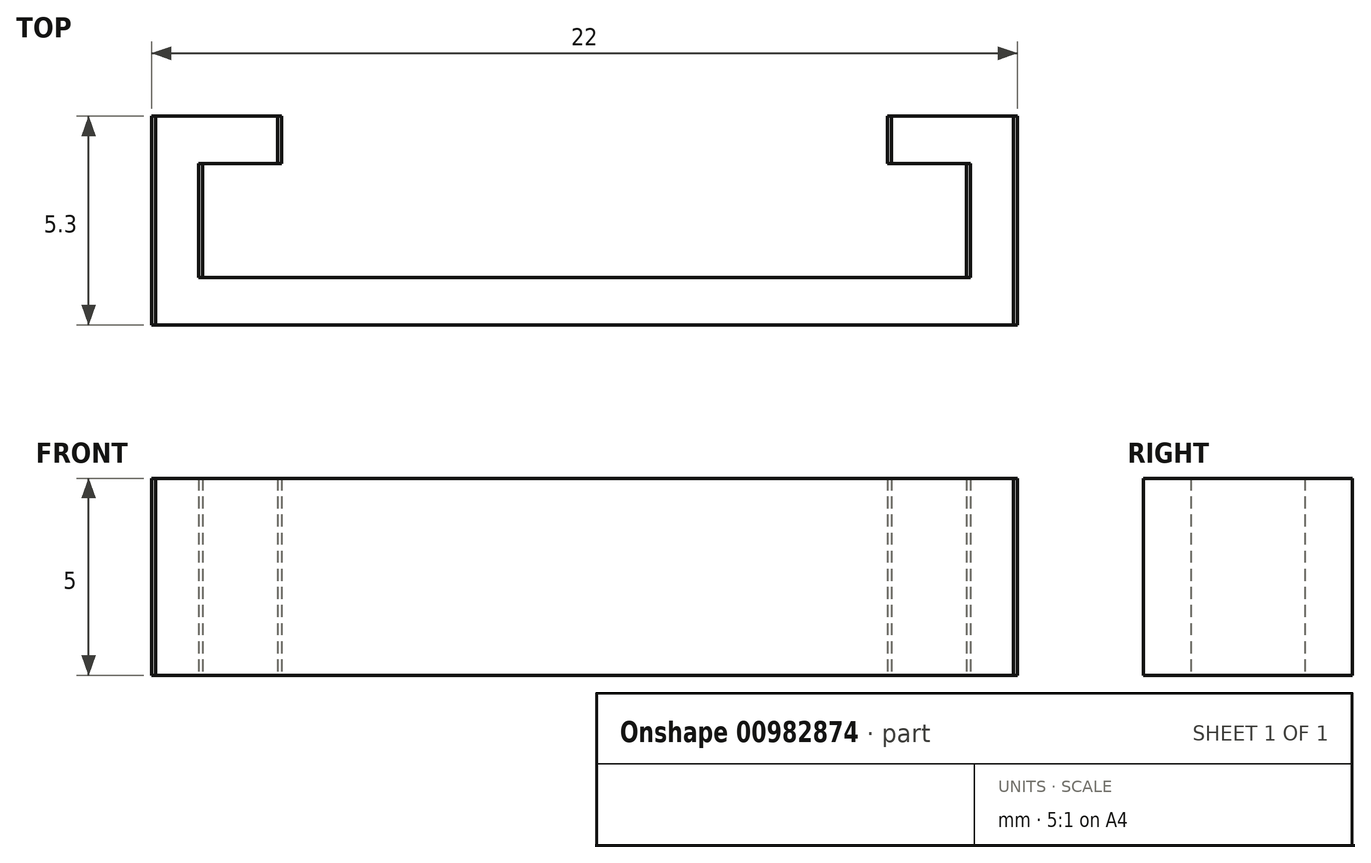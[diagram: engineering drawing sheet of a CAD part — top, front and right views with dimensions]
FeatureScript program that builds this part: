
annotation { "Feature Type Name" : "Feature", "Feature Type Description" : "" }
export const myFeature = defineFeature(function(context is Context, id is Id, definition is map)
    precondition{}
    {
        {
            var Q0;
            Q0=qCreatedBy(makeId("Top.planeOp"),FACE);
            var sketch = newSketch(context, id + "F0", { "sketchPlane" : qUnion([Q0])});
            skLineSegment(sketch, "E0", {"start": v(0, -39.9) * mm, "end": v(0, 36.9) * mm, "construction": true});
            skLineSegment(sketch, "E1", {"start": v(0, 0) * mm, "end": v(-11, 0) * mm});
            skLineSegment(sketch, "E2", {"start": v(-11, 0) * mm, "end": v(-11, 5.3) * mm});
            skLineSegment(sketch, "E3", {"start": v(-11, 5.3) * mm, "end": v(-7.8, 5.3) * mm});
            skLineSegment(sketch, "E4", {"start": v(-7.8, 5.3) * mm, "end": v(-7.8, 4.1) * mm});
            skLineSegment(sketch, "E5", {"start": v(-7.8, 4.1) * mm, "end": v(-9.8, 4.1) * mm});
            skLineSegment(sketch, "E6", {"start": v(-9.8, 4.1) * mm, "end": v(-9.8, 1.2) * mm});
            skLineSegment(sketch, "E7", {"start": v(-9.8, 1.2) * mm, "end": v(0, 1.2) * mm});
            skLineSegment(sketch, "E8", {"start": v(0, 1.2) * mm, "end": v(0, 0) * mm});
            skLineSegment(sketch, "E9.MirrorCS", {"start": v(9.8, 1.2) * mm, "end": v(0, 1.2) * mm});
            skLineSegment(sketch, "E10.MirrorCS", {"start": v(0, 0) * mm, "end": v(11, 0) * mm});
            skLineSegment(sketch, "E11.MirrorCS", {"start": v(11, 0) * mm, "end": v(11, 5.3) * mm});
            skLineSegment(sketch, "E12.MirrorCS", {"start": v(11, 5.3) * mm, "end": v(7.8, 5.3) * mm});
            skLineSegment(sketch, "E13.MirrorCS", {"start": v(7.8, 5.3) * mm, "end": v(7.8, 4.1) * mm});
            skLineSegment(sketch, "E14.MirrorCS", {"start": v(7.8, 4.1) * mm, "end": v(9.8, 4.1) * mm});
            skLineSegment(sketch, "E15.MirrorCS", {"start": v(9.8, 4.1) * mm, "end": v(9.8, 1.2) * mm});
            skSolve(sketch);
        }
        {
            var Q0;
            Q0=makeQuery(id+"F0.imprint","IMPRINT",FACE,{"disambiguationData":[TD([[makeQuery(id+"F0.imprint","IMPRINT",EDGE,{"derivedFrom":sQuery(id+"F0.wireOp",EDGE,"E1")}),-1.0]])]});
            var Q1;
            Q1=makeQuery(id+"F0.imprint","IMPRINT",FACE,{"disambiguationData":[TD([[makeQuery(id+"F0.imprint","IMPRINT",EDGE,{"derivedFrom":sQuery(id+"F0.wireOp",EDGE,"E8")}),1.0]])]});
            extrude(context, id + "F1", {"entities" : qUnion([Q0, Q1]), "depth" : 5 * mm, "offsetDistance" : 25 * mm});
        }
        {
            var Q0;
            Q0=qCreatedBy(makeId("Top.planeOp"),FACE);
            var sketch = newSketch(context, id + "F2", { "sketchPlane" : qUnion([Q0])});
            skLineSegment(sketch, "E16", {"start": v(0, -42.42) * mm, "end": v(0, 34.38) * mm, "construction": true});
            skLineSegment(sketch, "E17", {"start": v(0, 0) * mm, "end": v(-10.9, 0) * mm});
            skLineSegment(sketch, "E18", {"start": v(-10.9, 0) * mm, "end": v(-10.9, 5.3) * mm});
            skLineSegment(sketch, "E19", {"start": v(-10.9, 5.3) * mm, "end": v(-7.7, 5.3) * mm});
            skLineSegment(sketch, "E20", {"start": v(-7.7, 5.3) * mm, "end": v(-7.7, 4.1) * mm});
            skLineSegment(sketch, "E21", {"start": v(-7.7, 4.1) * mm, "end": v(-9.7, 4.1) * mm});
            skLineSegment(sketch, "E22", {"start": v(-9.7, 4.1) * mm, "end": v(-9.7, 1.2) * mm});
            skLineSegment(sketch, "E23", {"start": v(-9.7, 1.2) * mm, "end": v(0, 1.2) * mm});
            skLineSegment(sketch, "E24", {"start": v(0, 1.2) * mm, "end": v(0, 0) * mm});
            skLineSegment(sketch, "E25.MirrorCS", {"start": v(9.7, 1.2) * mm, "end": v(0, 1.2) * mm});
            skLineSegment(sketch, "E26.MirrorCS", {"start": v(0, 0) * mm, "end": v(10.9, 0) * mm});
            skLineSegment(sketch, "E27.MirrorCS", {"start": v(10.9, 0) * mm, "end": v(10.9, 5.3) * mm});
            skLineSegment(sketch, "E28.MirrorCS", {"start": v(10.9, 5.3) * mm, "end": v(7.7, 5.3) * mm});
            skLineSegment(sketch, "E29.MirrorCS", {"start": v(7.7, 5.3) * mm, "end": v(7.7, 4.1) * mm});
            skLineSegment(sketch, "E30.MirrorCS", {"start": v(7.7, 4.1) * mm, "end": v(9.7, 4.1) * mm});
            skLineSegment(sketch, "E31.MirrorCS", {"start": v(9.7, 4.1) * mm, "end": v(9.7, 1.2) * mm});
            skSolve(sketch);
        }
        {
            var Q0;
            Q0=makeQuery(id+"F2.imprint","IMPRINT",FACE,{"disambiguationData":[TD([[makeQuery(id+"F2.imprint","IMPRINT",EDGE,{"derivedFrom":sQuery(id+"F2.wireOp",EDGE,"E17")}),-1.0]])]});
            var Q1;
            Q1=makeQuery(id+"F2.imprint","IMPRINT",FACE,{"disambiguationData":[TD([[makeQuery(id+"F2.imprint","IMPRINT",EDGE,{"derivedFrom":sQuery(id+"F2.wireOp",EDGE,"E24")}),1.0]])]});
            extrude(context, id + "F3", {"entities" : qUnion([Q0, Q1]), "depth" : 5 * mm, "offsetDistance" : 25 * mm});
        }
    });
